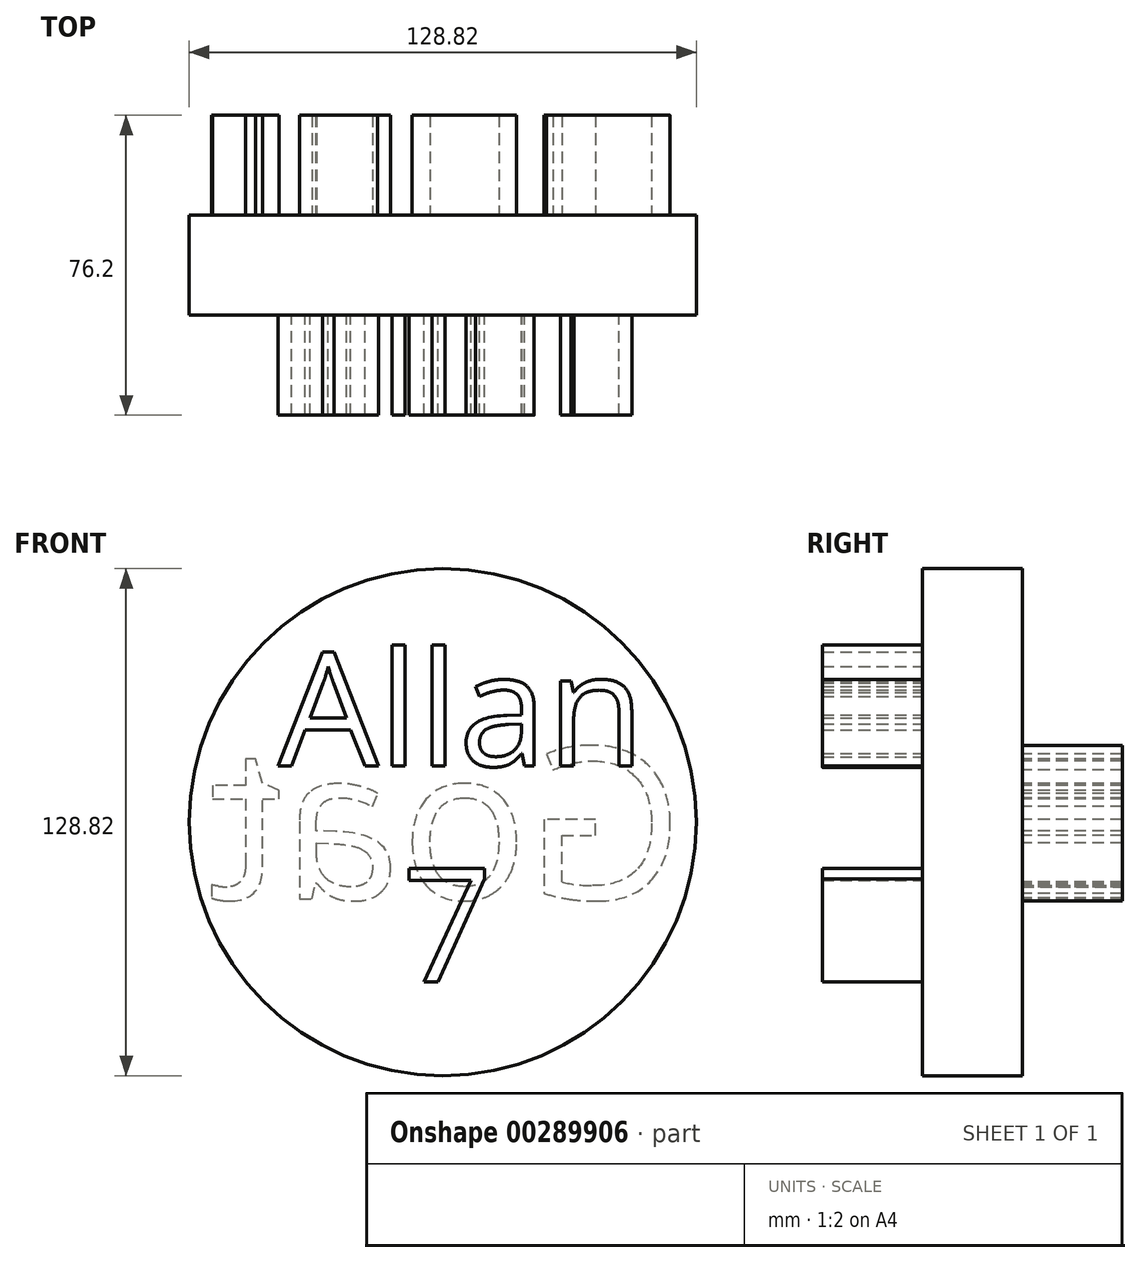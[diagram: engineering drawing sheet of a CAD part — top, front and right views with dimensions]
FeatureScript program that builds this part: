
annotation { "Feature Type Name" : "Feature", "Feature Type Description" : "" }
export const myFeature = defineFeature(function(context is Context, id is Id, definition is map)
    precondition{}
    {
        {
            var Q0;
            Q0=qCreatedBy(makeId("Front.planeOp"),FACE);
            var sketch = newSketch(context, id + "F0", { "sketchPlane" : qUnion([Q0])});
            skCircle(sketch, "E0", {"center": v(0, 0) * mm, "radius": 64.41 * mm});
            skSolve(sketch);
        }
        {
            var Q0;
            Q0 = qSketchRegion(id + "F0", true);
            extrude(context, id + "F1", {"entities" : qUnion([Q0]), "depth" : 25.4 * mm});
        }
        {
            var Q0;
            Q0=makeQuery(id+"F1.opExtrude","CAP_FACE",FACE,{"disambiguationData":[OSD([sQuery(id+"F0.wireOp",EDGE,"E0")])],"isStart":false});
            var sketch = newSketch(context, id + "F2", { "sketchPlane" : qUnion([Q0])});
            skText(sketch, "E1", { "text": "Allan\n   7", "fontName": "OpenSans-Regular.ttf"});
            const initialGuessF2  = {"E1": [-0.04186, 0.01432, 1, 0, 0.02904]};
            skSetInitialGuess(sketch, initialGuessF2);
            skSolve(sketch);
        }
        {
            var Q0;
            Q0 = qSketchRegion(id + "F2", true);
            extrude(context, id + "F3", {"entities" : qUnion([Q0]), "operationType" : NewBodyOperationType.ADD, "depth" : 25.4 * mm});
        }
        {
            var Q0;
            Q0=makeQuery(id+"F1.opExtrude","CAP_FACE",FACE,{"disambiguationData":[OSD([sQuery(id+"F0.wireOp",EDGE,"E0")])],"isStart":true});
            var sketch = newSketch(context, id + "F4", { "sketchPlane" : qUnion([Q0])});
            skText(sketch, "E2", { "text": "Goat", "fontName": "OpenSans-Regular.ttf"});
            const initialGuessF4  = {"E2": [-0.06108, -0.01953, 1, 0, 0.03885]};
            skSetInitialGuess(sketch, initialGuessF4);
            skSolve(sketch);
        }
        {
            var Q0;
            Q0 = qSketchRegion(id + "F4", true);
            extrude(context, id + "F5", {"entities" : qUnion([Q0]), "operationType" : NewBodyOperationType.ADD, "depth" : 25.4 * mm});
        }
    });
